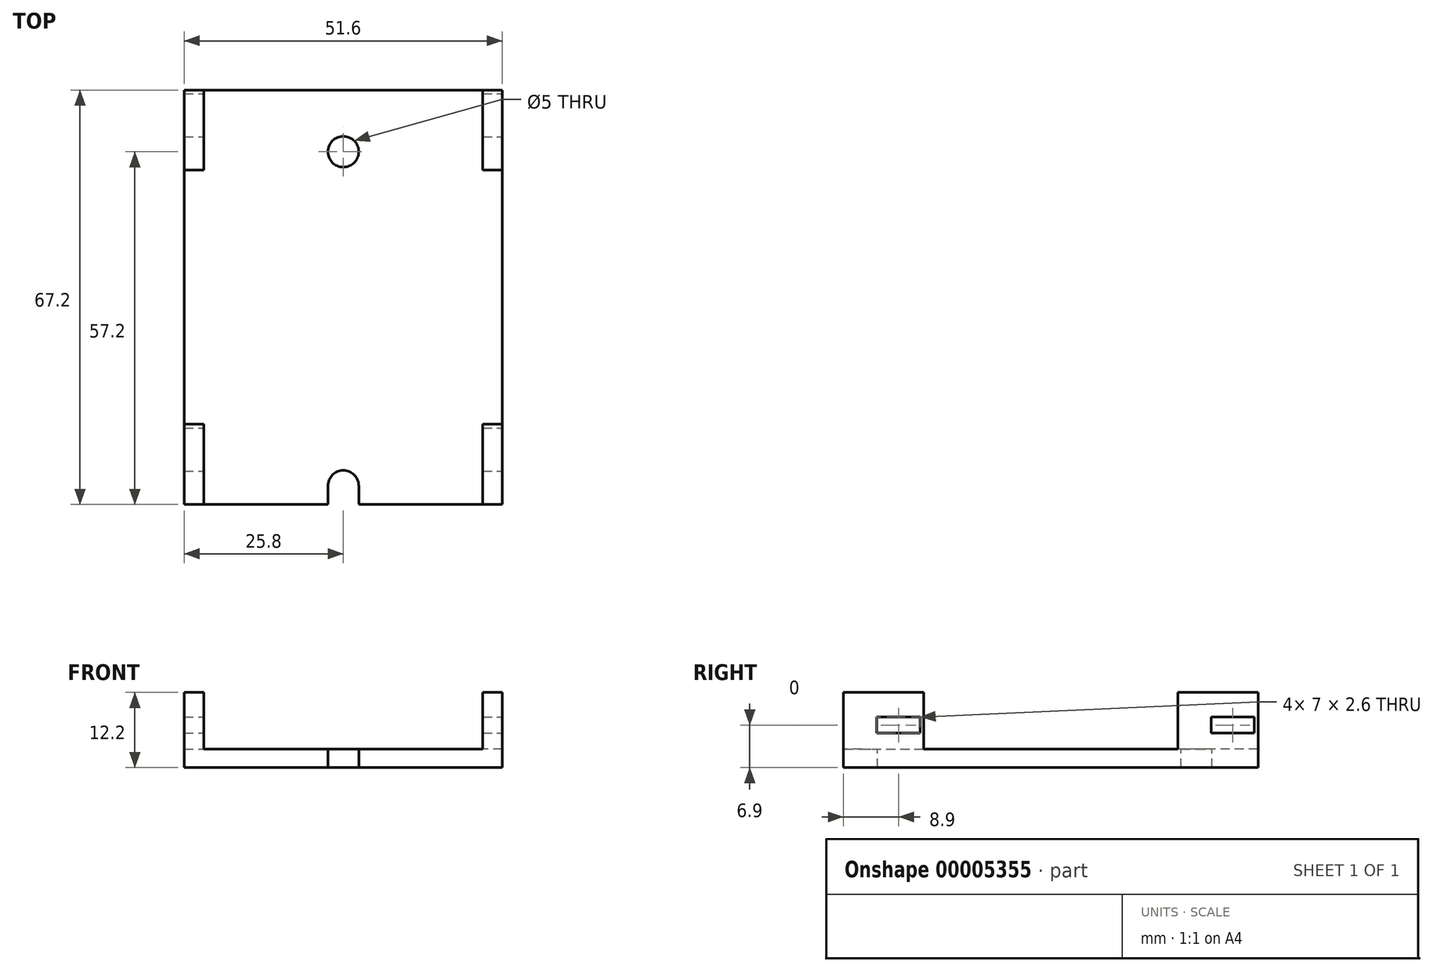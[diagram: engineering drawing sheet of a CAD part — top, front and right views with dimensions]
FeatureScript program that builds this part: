
annotation { "Feature Type Name" : "Feature", "Feature Type Description" : "" }
export const myFeature = defineFeature(function(context is Context, id is Id, definition is map)
    precondition{}
    {
        {
            var Q0;
            Q0=qCreatedBy(makeId("Top.planeOp"),FACE);
            var sketch = newSketch(context, id + "F0", { "sketchPlane" : qUnion([Q0])});
            skLineSegment(sketch, "E0.bottom", {"start": v(-25.8, 33.6) * mm, "end": v(25.8, 33.6) * mm});
            skLineSegment(sketch, "E0.top", {"start": v(-25.8, -33.6) * mm, "end": v(25.8, -33.6) * mm});
            skLineSegment(sketch, "E0.left", {"start": v(-25.8, 33.6) * mm, "end": v(-25.8, -33.6) * mm});
            skLineSegment(sketch, "E0.right", {"start": v(25.8, 33.6) * mm, "end": v(25.8, -33.6) * mm});
            skPoint(sketch, "E1", {"position": v(0, 33.6) * mm});
            skPoint(sketch, "E2", {"position": v(25.8, 0) * mm});
            skSolve(sketch);
        }
        {
            var Q0;
            Q0=makeQuery(id+"F0.imprint","IMPRINT",FACE,{"disambiguationData":[TD([[makeQuery(id+"F0.imprint","IMPRINT",EDGE,{"derivedFrom":sQuery(id+"F0.wireOp",EDGE,"E0.bottom")}),-1.0]])]});
            extrude(context, id + "F1", {"entities" : qUnion([Q0]), "depth" : 3 * mm});
        }
        {
            var Q0;
            Q0=makeQuery(id+"F1.opExtrude","CAP_FACE",FACE,{"disambiguationData":[OSD([sQuery(id+"F0.wireOp",EDGE,"E0.bottom"),sQuery(id+"F0.wireOp",EDGE,"E0.top"),sQuery(id+"F0.wireOp",EDGE,"E0.left"),sQuery(id+"F0.wireOp",EDGE,"E0.right")])],"isStart":false});
            var sketch = newSketch(context, id + "F2", { "sketchPlane" : qUnion([Q0])});
            skLineSegment(sketch, "E3.bottom", {"start": v(25.8, 33.6) * mm, "end": v(22.6, 33.6) * mm});
            skLineSegment(sketch, "E3.top", {"start": v(25.8, 20.6) * mm, "end": v(22.6, 20.6) * mm});
            skLineSegment(sketch, "E3.left", {"start": v(25.8, 33.6) * mm, "end": v(25.8, 20.6) * mm});
            skLineSegment(sketch, "E3.right", {"start": v(22.6, 33.6) * mm, "end": v(22.6, 20.6) * mm});
            skLineSegment(sketch, "E4.bottom", {"start": v(-25.8, -33.6) * mm, "end": v(-22.6, -33.6) * mm});
            skLineSegment(sketch, "E4.top", {"start": v(-25.8, -20.6) * mm, "end": v(-22.6, -20.6) * mm});
            skLineSegment(sketch, "E4.left", {"start": v(-25.8, -33.6) * mm, "end": v(-25.8, -20.6) * mm});
            skLineSegment(sketch, "E4.right", {"start": v(-22.6, -33.6) * mm, "end": v(-22.6, -20.6) * mm});
            skLineSegment(sketch, "E5.bottom", {"start": v(25.8, -33.6) * mm, "end": v(22.6, -33.6) * mm});
            skLineSegment(sketch, "E5.top", {"start": v(25.8, -20.6) * mm, "end": v(22.6, -20.6) * mm});
            skLineSegment(sketch, "E5.left", {"start": v(25.8, -33.6) * mm, "end": v(25.8, -20.6) * mm});
            skLineSegment(sketch, "E5.right", {"start": v(22.6, -33.6) * mm, "end": v(22.6, -20.6) * mm});
            skLineSegment(sketch, "E6.bottom", {"start": v(-25.8, 33.6) * mm, "end": v(-22.6, 33.6) * mm});
            skLineSegment(sketch, "E6.top", {"start": v(-25.8, 20.6) * mm, "end": v(-22.6, 20.6) * mm});
            skLineSegment(sketch, "E6.left", {"start": v(-25.8, 33.6) * mm, "end": v(-25.8, 20.6) * mm});
            skLineSegment(sketch, "E6.right", {"start": v(-22.6, 33.6) * mm, "end": v(-22.6, 20.6) * mm});
            skSolve(sketch);
        }
        {
            var Q0;
            Q0 = qSketchRegion(id + "F2", true);
            extrude(context, id + "F3", {"entities" : qUnion([Q0]), "operationType" : NewBodyOperationType.ADD, "depth" : 9.2 * mm});
        }
        {
            var Q0;
            Q0=makeQuery(id+"F3.boolean.opBoolean","MERGE",FACE,{"derivedFrom":[makeQuery(id+"F1.opExtrude","SWEPT_FACE",FACE,{"disambiguationData":[OSD([sQuery(id+"F0.wireOp",EDGE,"E0.right")])]}),makeQuery(id+"F3.opExtrude","SWEPT_FACE",FACE,{"disambiguationData":[OSD([sQuery(id+"F2.wireOp",EDGE,"E3.left")])]}),makeQuery(id+"F3.opExtrude","SWEPT_FACE",FACE,{"disambiguationData":[OSD([sQuery(id+"F2.wireOp",EDGE,"E5.left")])]})]});
            var sketch = newSketch(context, id + "F4", { "sketchPlane" : qUnion([Q0])});
            skLineSegment(sketch, "E7.bottom", {"start": v(33, 5.6) * mm, "end": v(26, 5.6) * mm});
            skLineSegment(sketch, "E7.top", {"start": v(33, 8.2) * mm, "end": v(26, 8.2) * mm});
            skLineSegment(sketch, "E7.left", {"start": v(33, 5.6) * mm, "end": v(33, 8.2) * mm});
            skLineSegment(sketch, "E7.right", {"start": v(26, 5.6) * mm, "end": v(26, 8.2) * mm});
            skLineSegment(sketch, "E8.bottom", {"start": v(-21.2, 5.6) * mm, "end": v(-28.2, 5.6) * mm});
            skLineSegment(sketch, "E8.top", {"start": v(-21.2, 8.2) * mm, "end": v(-28.2, 8.2) * mm});
            skLineSegment(sketch, "E8.left", {"start": v(-21.2, 5.6) * mm, "end": v(-21.2, 8.2) * mm});
            skLineSegment(sketch, "E8.right", {"start": v(-28.2, 5.6) * mm, "end": v(-28.2, 8.2) * mm});
            skSolve(sketch);
        }
        {
            var Q0;
            Q0 = qSketchRegion(id + "F4", true);
            extrude(context, id + "F5", {"entities" : qUnion([Q0]), "operationType" : NewBodyOperationType.REMOVE, "endBound" : BoundingType.THROUGH_ALL, "oppositeDirection" : true, "depth" : 25 * mm});
        }
        {
            var Q0;
            Q0=makeQuery(id+"F1.opExtrude","CAP_FACE",FACE,{"disambiguationData":[OSD([sQuery(id+"F0.wireOp",EDGE,"E0.bottom"),sQuery(id+"F0.wireOp",EDGE,"E0.top"),sQuery(id+"F0.wireOp",EDGE,"E0.left"),sQuery(id+"F0.wireOp",EDGE,"E0.right")])],"isStart":false});
            var sketch = newSketch(context, id + "F6", { "sketchPlane" : qUnion([Q0])});
            skCircle(sketch, "E9", {"center": v(0, 23.6) * mm, "radius": 2.5 * mm});
            skCircle(sketch, "E10", {"center": v(0, -30.6) * mm, "radius": 2.5 * mm});
            skLineSegment(sketch, "E11", {"start": v(-2.5, -30.6) * mm, "end": v(-2.5, -33.6) * mm});
            skLineSegment(sketch, "E12", {"start": v(-2.5, -33.6) * mm, "end": v(2.5, -33.6) * mm});
            skLineSegment(sketch, "E13", {"start": v(2.5, -33.6) * mm, "end": v(2.5, -30.6) * mm});
            skSolve(sketch);
        }
        {
            var Q0;
            Q0 = qSketchRegion(id + "F6", true);
            extrude(context, id + "F7", {"entities" : qUnion([Q0]), "operationType" : NewBodyOperationType.REMOVE, "endBound" : BoundingType.THROUGH_ALL, "oppositeDirection" : true, "depth" : 25 * mm});
        }
    });
